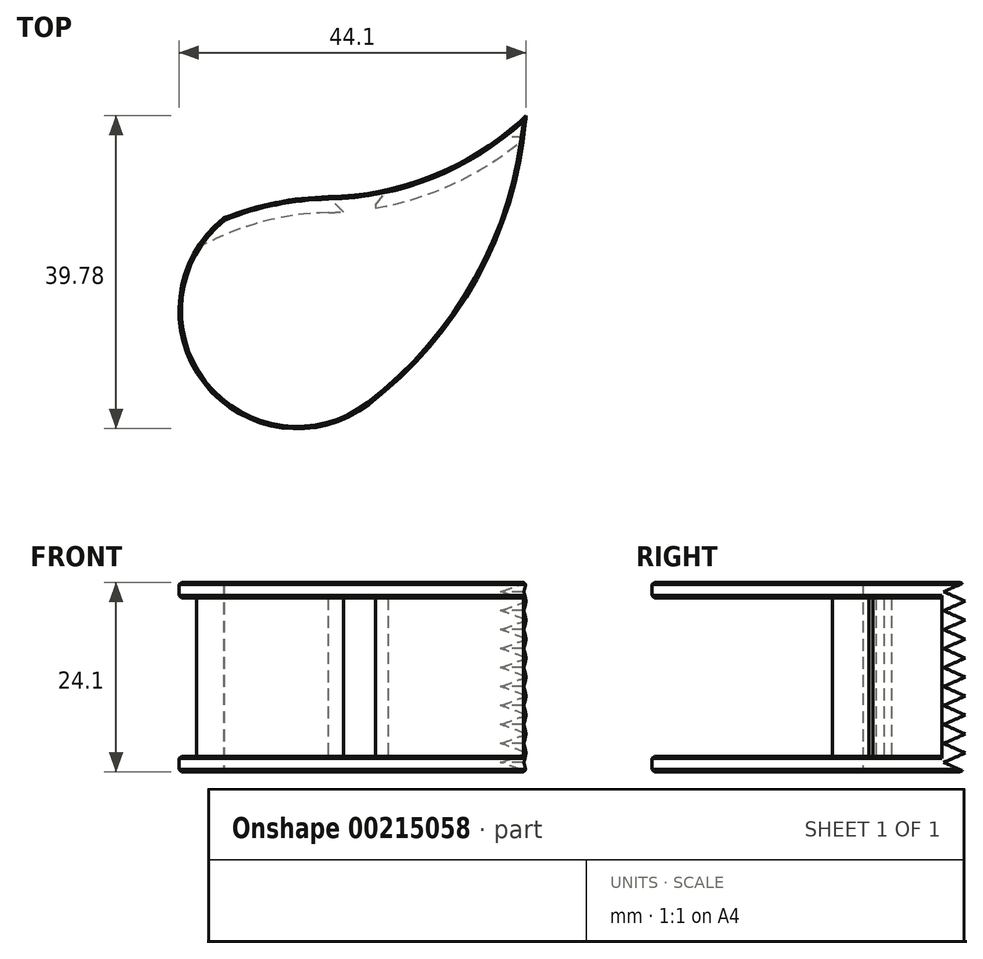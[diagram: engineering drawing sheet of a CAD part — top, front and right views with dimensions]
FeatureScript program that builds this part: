
annotation { "Feature Type Name" : "Feature", "Feature Type Description" : "" }
export const myFeature = defineFeature(function(context is Context, id is Id, definition is map)
    precondition{}
    {
        {
            assignVariable(context, id + "F0", {"name" : "PrintOffset", "anyValue" : 0.3});
        }
        {
            assignVariable(context, id + "F1", {"name" : "TapeWidth", "anyValue" : 19.5});
        }
        {
            assignVariable(context, id + "F2", {"name" : "WallThickness", "anyValue" : 2});
        }
        {
            assignVariable(context, id + "F3", {"name" : "TotalWidth", "anyValue" : (getVariable(context, 'TapeWidth') + (2 * getVariable(context, 'WallThickness')) + (2 * getVariable(context, 'PrintOffset'))) * mm});
        }
        {
            var Q0;
            Q0=qCreatedBy(makeId("Top.planeOp"),FACE);
            var sketch = newSketch(context, id + "F4", { "sketchPlane" : qUnion([Q0])});
            skArc(sketch, "E0", {"start": v(-0.7, 37.5) * mm, "mid": v(-10.28, -36.06) * mm, "end": v(20.36, 31.49) * mm});
            skArc(sketch, "E1", {"start": v(-0.7, 37.5) * mm, "mid": v(12.83, 40.3) * mm, "end": v(24.43, 47.8) * mm});
            skArc(sketch, "E2", {"start": v(-13.95, 34.8) * mm, "mid": v(-1.69, 8.33) * mm, "end": v(-0.7, 37.5) * mm});
            skArc(sketch, "E3", {"start": v(4.45, 11.12) * mm, "mid": v(18.34, 27.34) * mm, "end": v(24.43, 47.8) * mm});
            skSolve(sketch);
        }
        {
            var Q0;
            {var subQ0=sQuery(id+"F4.wireOp",EDGE,"E2");var subQ1=sQuery(id+"F4.wireOp",EDGE,"E0");var subQ3=makeQuery(id+"F4.imprint","INTERSECT",VERTEX,{"derivedFrom":[subQ1,subQ0]});Q0=makeQuery(id+"F4.imprint","IMPRINT",FACE,{"disambiguationData":[TD([[makeQuery(id+"F4.imprint","IMPRINT",EDGE,{"disambiguationData":[TD([[subQ3,-1.0]])],"derivedFrom":subQ0}),1.0]])]});}
            var Q1;
            {var subQ0=sQuery(id+"F4.wireOp",EDGE,"E1");Q1=makeQuery(id+"F4.imprint","IMPRINT",FACE,{"disambiguationData":[TD([[makeQuery(id+"F4.imprint","IMPRINT",EDGE,{"derivedFrom":subQ0}),-1.0]])]});}
            extrude(context, id + "F5", {"entities" : qUnion([Q0, Q1]), "depth" : getVariable(context, 'TotalWidth')});
        }
        {
            var Q0;
            Q0=makeQuery(id+"F5.opExtrude","SWEPT_FACE",FACE,{"disambiguationData":[OSD([sQuery(id+"F4.wireOp",EDGE,"E3")])]});
            var Q1;
            Q1=makeQuery(id+"F5.opExtrude","SWEPT_FACE",FACE,{"disambiguationData":[OSD([sQuery(id+"F4.wireOp",EDGE,"E2")])]});
            shell(context, id + "F6", {"entities" : qUnion([Q0, Q1]), "thickness" : (getVariable(context, 'WallThickness')) * mm});
        }
        {
            var Q0;
            Q0=qCreatedBy(makeId("Front.planeOp"),FACE);
            var sketch = newSketch(context, id + "F7", { "sketchPlane" : qUnion([Q0])});
            skLineSegment(sketch, "E4.0", {"start": v(24.43, 24.1) * mm, "end": v(24.43, 0) * mm, "construction": true});
            skLineSegment(sketch, "E4.1", {"start": v(-0.7, 24.1) * mm, "end": v(-0.7, 0) * mm, "construction": true});
            skLineSegment(sketch, "E4.2", {"start": v(-13.95, 24.1) * mm, "end": v(-13.95, 0) * mm, "construction": true});
            skLineSegment(sketch, "E5", {"start": v(-13.95, 24.1) * mm, "end": v(-0.7, 24.1) * mm, "construction": true});
            skLineSegment(sketch, "E6", {"start": v(-0.7, 0) * mm, "end": v(-13.95, 0) * mm, "construction": true});
            skLineSegment(sketch, "E7.1", {"start": v(1.3, 22.1) * mm, "end": v(5.3, 22.1) * mm});
            skLineSegment(sketch, "E7.2", {"start": v(1.3, 22.1) * mm, "end": v(1.3, 2) * mm});
            skLineSegment(sketch, "E7.3", {"start": v(5.3, 2) * mm, "end": v(1.3, 2) * mm});
            skLineSegment(sketch, "E8", {"start": v(5.3, 2) * mm, "end": v(5.3, 22.1) * mm});
            skSolve(sketch);
        }
        {
            var Q0;
            Q0=makeQuery(id+"F7.imprint","IMPRINT",FACE,{"disambiguationData":[TD([[makeQuery(id+"F7.imprint","IMPRINT",EDGE,{"derivedFrom":sQuery(id+"F7.wireOp",EDGE,"E7.1")}),-1.0]])]});
            extrude(context, id + "F8", {"entities" : qUnion([Q0]), "operationType" : NewBodyOperationType.REMOVE, "endBound" : BoundingType.THROUGH_ALL, "oppositeDirection" : true, "depth" : 25 * mm});
        }
        {
            var Q0;
            Q0=qCreatedBy(makeId("Right.planeOp"),FACE);
            var sketch = newSketch(context, id + "F9", { "sketchPlane" : qUnion([Q0])});
            skLineSegment(sketch, "E9.0", {"start": v(47.8, 24.1) * mm, "end": v(47.8, 0) * mm});
            skLineSegment(sketch, "E10", {"start": v(47.8, 0) * mm, "end": v(45.06, 1.2) * mm});
            skLineSegment(sketch, "E11", {"start": v(45.06, 1.2) * mm, "end": v(47.8, 2.41) * mm});
            skLineSegment(sketch, "E12.1.0.0", {"start": v(45.06, 3.62) * mm, "end": v(47.8, 4.82) * mm});
            skLineSegment(sketch, "E12.1.0.1", {"start": v(47.8, 2.41) * mm, "end": v(45.06, 3.62) * mm});
            skLineSegment(sketch, "E12.2.0.0", {"start": v(45.06, 6.03) * mm, "end": v(47.8, 7.23) * mm});
            skLineSegment(sketch, "E12.2.0.1", {"start": v(47.8, 4.82) * mm, "end": v(45.06, 6.03) * mm});
            skLineSegment(sketch, "E12.direction1", {"start": v(45.06, 1.2) * mm, "end": v(45.06, 3.62) * mm, "construction": true});
            skLineSegment(sketch, "E13.0.3.0", {"start": v(45.06, 8.44) * mm, "end": v(47.8, 9.64) * mm});
            skLineSegment(sketch, "E13.3.3.0", {"start": v(47.8, 7.23) * mm, "end": v(45.06, 8.44) * mm});
            skLineSegment(sketch, "E13.0.4.0", {"start": v(45.06, 10.85) * mm, "end": v(47.8, 12.05) * mm});
            skLineSegment(sketch, "E13.3.4.0", {"start": v(47.8, 9.64) * mm, "end": v(45.06, 10.85) * mm});
            skLineSegment(sketch, "E13.0.5.0", {"start": v(45.06, 13.26) * mm, "end": v(47.8, 14.46) * mm});
            skLineSegment(sketch, "E13.3.5.0", {"start": v(47.8, 12.05) * mm, "end": v(45.06, 13.26) * mm});
            skLineSegment(sketch, "E13.0.6.0", {"start": v(45.06, 15.67) * mm, "end": v(47.8, 16.87) * mm});
            skLineSegment(sketch, "E13.3.6.0", {"start": v(47.8, 14.46) * mm, "end": v(45.06, 15.67) * mm});
            skLineSegment(sketch, "E13.0.7.0", {"start": v(45.06, 18.08) * mm, "end": v(47.8, 19.28) * mm});
            skLineSegment(sketch, "E13.3.7.0", {"start": v(47.8, 16.87) * mm, "end": v(45.06, 18.08) * mm});
            skLineSegment(sketch, "E13.0.8.0", {"start": v(45.06, 20.49) * mm, "end": v(47.8, 21.7) * mm});
            skLineSegment(sketch, "E13.3.8.0", {"start": v(47.8, 19.28) * mm, "end": v(45.06, 20.48) * mm});
            skLineSegment(sketch, "E13.0.9.0", {"start": v(45.06, 22.9) * mm, "end": v(47.8, 24.1) * mm});
            skLineSegment(sketch, "E13.3.9.0", {"start": v(47.8, 21.7) * mm, "end": v(45.06, 22.9) * mm});
            skSolve(sketch);
        }
        {
            var Q0;
            Q0 = qSketchRegion(id + "F9", true);
            var Q1;
            Q1 = qConstructionFilter(qBodyType(qCreatedBy(id + "F9" ,EDGE), BodyType.WIRE), ConstructionObject.NO);
            extrude(context, id + "F10", {"entities" : qUnion([Q0]), "operationType" : NewBodyOperationType.REMOVE, "surfaceEntities" : qUnion([Q1]), "endBound" : BoundingType.THROUGH_ALL, "depth" : 25 * mm});
        }
        {
            var Q0;
            Q0=makeQuery(id+"F8.boolean.opBoolean","INTERSECT",EDGE,{"derivedFrom":[makeQuery(id+"F5.opExtrude","SWEPT_FACE",FACE,{"disambiguationData":[OSD([sQuery(id+"F4.wireOp",EDGE,"E1")])]}),makeQuery(id+"F8.opExtrude","SWEPT_FACE",FACE,{"disambiguationData":[OSD([sQuery(id+"F7.wireOp",EDGE,"E8")])]})]});
            var Q1;
            Q1=makeQuery(id+"F8.boolean.opBoolean","INTERSECT",EDGE,{"derivedFrom":[makeQuery(id+"F5.opExtrude","SWEPT_FACE",FACE,{"disambiguationData":[OSD([sQuery(id+"F4.wireOp",EDGE,"E1")])]}),makeQuery(id+"F8.opExtrude","SWEPT_FACE",FACE,{"disambiguationData":[OSD([sQuery(id+"F7.wireOp",EDGE,"E7.2")])]})]});
            chamfer(context, id + "F11", {"entities" : qUnion([Q0, Q1]), "width" : (getVariable(context, 'WallThickness')) * mm, "tangentPropagation" : true});
        }
        {
            var Q0;
            Q0=makeQuery(id+"F5.opExtrude","CAP_FACE",FACE,{"disambiguationData":[OSD([sQuery(id+"F4.wireOp",EDGE,"E0"),sQuery(id+"F4.wireOp",EDGE,"E1"),sQuery(id+"F4.wireOp",EDGE,"E2"),sQuery(id+"F4.wireOp",EDGE,"E3")])],"isStart":false});
            var Q1;
            Q1=makeQuery(id+"F5.opExtrude","CAP_FACE",FACE,{"disambiguationData":[OSD([sQuery(id+"F4.wireOp",EDGE,"E0"),sQuery(id+"F4.wireOp",EDGE,"E1"),sQuery(id+"F4.wireOp",EDGE,"E2"),sQuery(id+"F4.wireOp",EDGE,"E3")])],"isStart":true});
            var Q2;
            {var subQ0=sQuery(id+"F4.wireOp",EDGE,"E3");Q2=makeQuery(id+"F6.opShell","OFFSET_EDGE",EDGE,{"disambiguationData":[OSD([subQ0]),TDD([makeQuery(id+"F5.opExtrude","CAP_EDGE",EDGE,{"disambiguationData":[OSD([subQ0])],"isStart":true})])]});}
            var Q3;
            {var subQ0=sQuery(id+"F4.wireOp",EDGE,"E2");Q3=makeQuery(id+"F6.opShell","OFFSET_EDGE",EDGE,{"disambiguationData":[OSD([subQ0]),TDD([makeQuery(id+"F5.opExtrude","CAP_EDGE",EDGE,{"disambiguationData":[OSD([subQ0])],"isStart":true})])]});}
            var Q4;
            {var subQ0=sQuery(id+"F4.wireOp",EDGE,"E3");Q4=makeQuery(id+"F6.opShell","OFFSET_EDGE",EDGE,{"disambiguationData":[OSD([subQ0]),TDD([makeQuery(id+"F5.opExtrude","CAP_EDGE",EDGE,{"disambiguationData":[OSD([subQ0])],"isStart":false})])]});}
            var Q5;
            {var subQ0=sQuery(id+"F4.wireOp",EDGE,"E2");Q5=makeQuery(id+"F6.opShell","OFFSET_EDGE",EDGE,{"disambiguationData":[OSD([subQ0]),TDD([makeQuery(id+"F5.opExtrude","CAP_EDGE",EDGE,{"disambiguationData":[OSD([subQ0])],"isStart":false})])]});}
            var Q6;
            Q6=makeQuery(id+"F5.opExtrude","SWEPT_EDGE",EDGE,{"disambiguationData":[OSD([sQuery(id+"F4.wireOp",EDGE,"E0"),sQuery(id+"F4.wireOp",EDGE,"E2")])]});
            chamfer(context, id + "F12", {"entities" : qUnion([Q0, Q1, Q2, Q3, Q4, Q5, Q6]), "width" : (getVariable(context, 'PrintOffset')) * mm, "tangentPropagation" : true});
        }
    });
